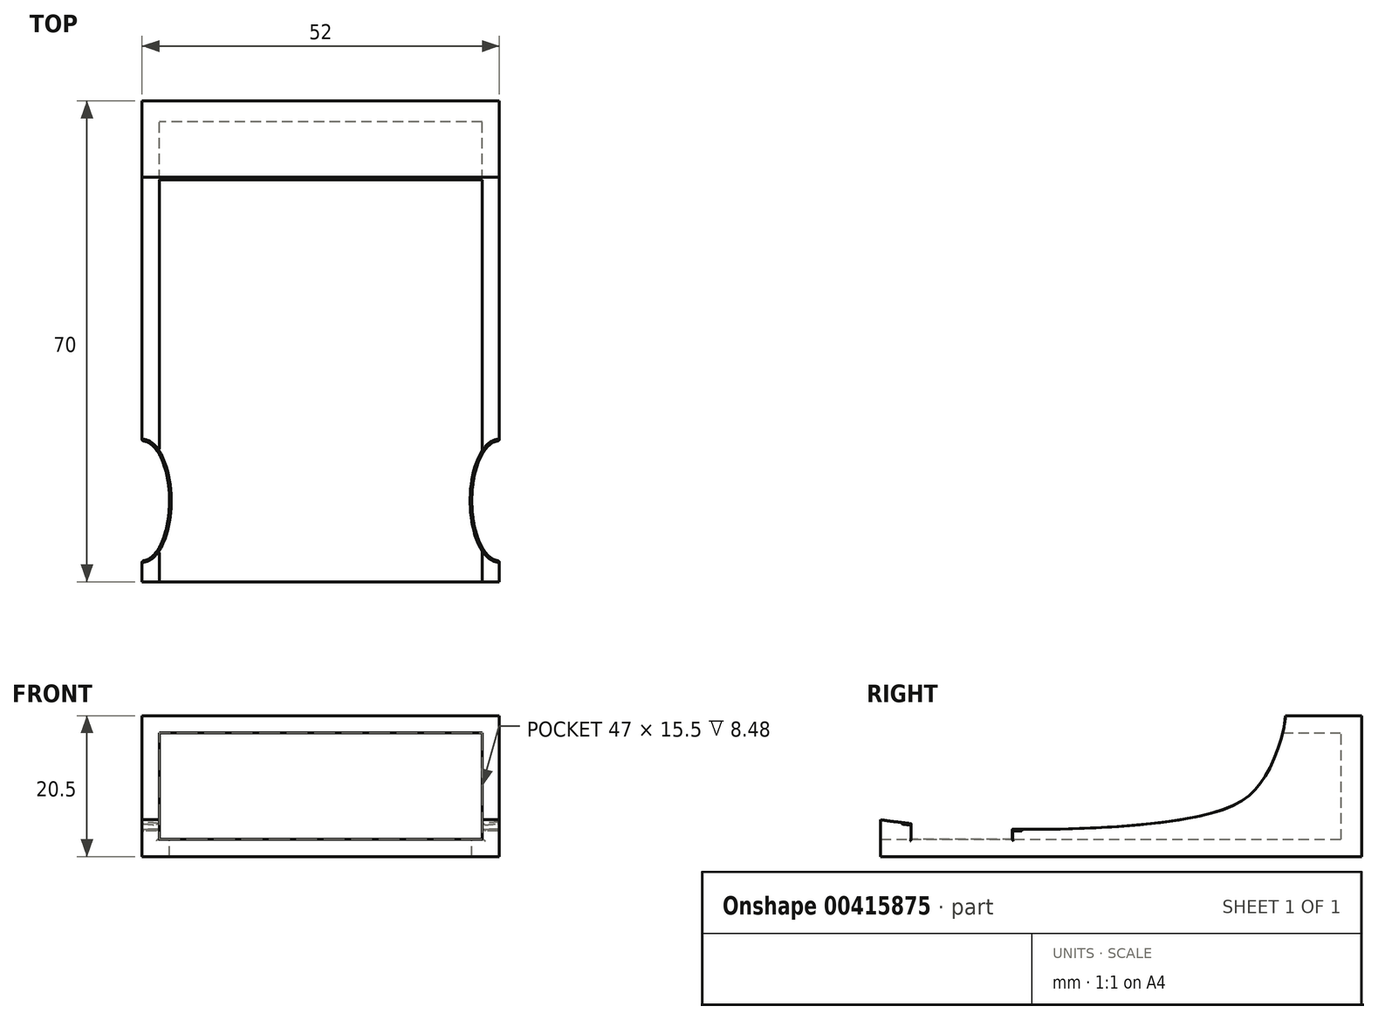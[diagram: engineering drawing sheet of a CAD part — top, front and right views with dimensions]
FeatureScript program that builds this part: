
annotation { "Feature Type Name" : "Feature", "Feature Type Description" : "" }
export const myFeature = defineFeature(function(context is Context, id is Id, definition is map)
    precondition{}
    {
        {
            var Q0;
            Q0=qCreatedBy(makeId("Front.planeOp"),FACE);
            var sketch = newSketch(context, id + "F0", { "sketchPlane" : qUnion([Q0])});
            skLineSegment(sketch, "E0.left", {"start": v(0, 0) * mm, "end": v(0, 0) * mm});
            skLineSegment(sketch, "E1", {"start": v(0, 0) * mm, "end": v(52, 0) * mm});
            skLineSegment(sketch, "E2", {"start": v(52, 0) * mm, "end": v(52, 20.5) * mm});
            skLineSegment(sketch, "E3", {"start": v(52, 20.5) * mm, "end": v(0, 20.5) * mm});
            skLineSegment(sketch, "E4", {"start": v(0, 20.5) * mm, "end": v(0, 0) * mm});
            skLineSegment(sketch, "E5", {"start": v(2.5, 2.5) * mm, "end": v(2.5, 18) * mm});
            skLineSegment(sketch, "E6", {"start": v(2.5, 18) * mm, "end": v(49.5, 18) * mm});
            skLineSegment(sketch, "E7", {"start": v(49.5, 18) * mm, "end": v(49.5, 2.5) * mm});
            skLineSegment(sketch, "E8", {"start": v(49.5, 2.5) * mm, "end": v(2.5, 2.5) * mm});
            skSolve(sketch);
        }
        {
            var Q0;
            Q0 = qSketchRegion(id + "F0", true);
            extrude(context, id + "F1", {"entities" : qUnion([Q0]), "depth" : 67 * mm});
        }
        {
            var Q0;
            Q0=makeQuery(id+"F0.imprint","IMPRINT",FACE,{"disambiguationData":[TD([[makeQuery(id+"F0.imprint","IMPRINT",EDGE,{"derivedFrom":sQuery(id+"F0.wireOp",EDGE,"E5")}),-1.0]])]});
            var Q1;
            Q1=makeQuery(id+"F0.imprint","IMPRINT",FACE,{"disambiguationData":[TD([[makeQuery(id+"F0.imprint","IMPRINT",EDGE,{"derivedFrom":sQuery(id+"F0.wireOp",EDGE,"E1")}),1.0]])]});
            extrude(context, id + "F2", {"entities" : qUnion([Q0, Q1]), "operationType" : NewBodyOperationType.ADD, "oppositeDirection" : true, "depth" : 3 * mm});
        }
        {
            var Q0;
            Q0=qCreatedBy(makeId("Right.planeOp"),FACE);
            var sketch = newSketch(context, id + "F3", { "sketchPlane" : qUnion([Q0])});
            skFitSpline(sketch, "E9", {"points": [v(-11.3, 29.1) * mm, v(-10.17, 13.31) * mm, v(-20.54, 5.9) * mm, v(-76.25, 7.4) * mm, v(-83.86, 15.4) * mm, v(-74.07, 28.56) * mm, v(-11.3, 29.1) * mm]});
            skSolve(sketch);
        }
        {
            var Q0;
            Q0=makeQuery(id+"F3.imprint","IMPRINT",FACE,{"disambiguationData":[TD([[makeQuery(id+"F3.imprint","IMPRINT",EDGE,{"derivedFrom":sQuery(id+"F3.wireOp",EDGE,"E9")}),-1.0]])]});
            extrude(context, id + "F4", {"entities" : qUnion([Q0]), "operationType" : NewBodyOperationType.REMOVE, "depth" : 70 * mm});
        }
        {
            var Q0;
            Q0=qCreatedBy(makeId("Top.planeOp"),FACE);
            var sketch = newSketch(context, id + "F5", { "sketchPlane" : qUnion([Q0])});
            skEllipse(sketch, "E10", {"center": v(0, -55.2) * mm, "majorRadius": 8.73 * mm, "minorRadius": 3.98 * mm, "majorAxis": v(0, -1)});
            skLineSegment(sketch, "E11", {"start": v(0, -55.2) * mm, "end": v(52, -55.2) * mm});
            skEllipse(sketch, "E12", {"center": v(52, -55.2) * mm, "majorRadius": 8.73 * mm, "minorRadius": 3.98 * mm, "majorAxis": v(0, -1)});
            skSolve(sketch);
        }
        {
            var Q0;
            Q0=makeQuery(id+"F5.imprint","IMPRINT",FACE,{"disambiguationData":[TD([[makeQuery(id+"F5.imprint","IMPRINT",EDGE,{"derivedFrom":sQuery(id+"F5.wireOp",EDGE,"E10")}),1.0]])]});
            var Q1;
            Q1=makeQuery(id+"F5.imprint","IMPRINT",FACE,{"disambiguationData":[TD([[makeQuery(id+"F5.imprint","IMPRINT",EDGE,{"derivedFrom":sQuery(id+"F5.wireOp",EDGE,"E12")}),1.0]])]});
            extrude(context, id + "F6", {"entities" : qUnion([Q0, Q1]), "operationType" : NewBodyOperationType.REMOVE, "depth" : 25 * mm});
        }
        {
            var Q0;
            Q0=makeQuery(id+"F6.boolean.opBoolean","INTERSECT",EDGE,{"derivedFrom":[makeQuery(id+"F1.opExtrude","SWEPT_FACE",FACE,{"disambiguationData":[OSD([sQuery(id+"F0.wireOp",EDGE,"E8")])]}),makeQuery(id+"F6.opExtrude","SWEPT_FACE",FACE,{"disambiguationData":[OSD([sQuery(id+"F5.wireOp",EDGE,"E10")])]})]});
            var Q1;
            Q1=makeQuery(id+"F6.boolean.opBoolean","INTERSECT",EDGE,{"disambiguationData":[OD(1.0)],"derivedFrom":[makeQuery(id+"F4.boolean.opBoolean","COPY",FACE,{"derivedFrom":makeQuery(id+"F4.opExtrude","SWEPT_FACE",FACE,{"disambiguationData":[OSD([sQuery(id+"F3.wireOp",EDGE,"E9")])]})}),makeQuery(id+"F6.opExtrude","SWEPT_FACE",FACE,{"disambiguationData":[OSD([sQuery(id+"F5.wireOp",EDGE,"E10")])]})]});
            var Q2;
            Q2=makeQuery(id+"F6.boolean.opBoolean","INTERSECT",EDGE,{"disambiguationData":[OD(0.0)],"derivedFrom":[makeQuery(id+"F4.boolean.opBoolean","COPY",FACE,{"derivedFrom":makeQuery(id+"F4.opExtrude","SWEPT_FACE",FACE,{"disambiguationData":[OSD([sQuery(id+"F3.wireOp",EDGE,"E9")])]})}),makeQuery(id+"F6.opExtrude","SWEPT_FACE",FACE,{"disambiguationData":[OSD([sQuery(id+"F5.wireOp",EDGE,"E10")])]})]});
            var Q3;
            Q3=makeQuery(id+"F6.boolean.opBoolean","INTERSECT",EDGE,{"disambiguationData":[OD(0.0)],"derivedFrom":[makeQuery(id+"F1.opExtrude","SWEPT_FACE",FACE,{"disambiguationData":[OSD([sQuery(id+"F0.wireOp",EDGE,"E5")])]}),makeQuery(id+"F6.opExtrude","SWEPT_FACE",FACE,{"disambiguationData":[OSD([sQuery(id+"F5.wireOp",EDGE,"E10")])]})]});
            var Q4;
            Q4=makeQuery(id+"F6.boolean.opBoolean","INTERSECT",EDGE,{"disambiguationData":[OD(1.0)],"derivedFrom":[makeQuery(id+"F4.boolean.opBoolean","COPY",FACE,{"derivedFrom":makeQuery(id+"F4.opExtrude","SWEPT_FACE",FACE,{"disambiguationData":[OSD([sQuery(id+"F3.wireOp",EDGE,"E9")])]})}),makeQuery(id+"F6.opExtrude","SWEPT_FACE",FACE,{"disambiguationData":[OSD([sQuery(id+"F5.wireOp",EDGE,"E12")])]})]});
            var Q5;
            Q5=makeQuery(id+"F6.boolean.opBoolean","INTERSECT",EDGE,{"derivedFrom":[makeQuery(id+"F1.opExtrude","SWEPT_FACE",FACE,{"disambiguationData":[OSD([sQuery(id+"F0.wireOp",EDGE,"E8")])]}),makeQuery(id+"F6.opExtrude","SWEPT_FACE",FACE,{"disambiguationData":[OSD([sQuery(id+"F5.wireOp",EDGE,"E12")])]})]});
            var Q6;
            Q6=makeQuery(id+"F6.boolean.opBoolean","INTERSECT",EDGE,{"disambiguationData":[OD(0.0)],"derivedFrom":[makeQuery(id+"F4.boolean.opBoolean","COPY",FACE,{"derivedFrom":makeQuery(id+"F4.opExtrude","SWEPT_FACE",FACE,{"disambiguationData":[OSD([sQuery(id+"F3.wireOp",EDGE,"E9")])]})}),makeQuery(id+"F6.opExtrude","SWEPT_FACE",FACE,{"disambiguationData":[OSD([sQuery(id+"F5.wireOp",EDGE,"E12")])]})]});
            var Q7;
            Q7=makeQuery(id+"F6.boolean.opBoolean","INTERSECT",EDGE,{"disambiguationData":[OD(1.0)],"derivedFrom":[makeQuery(id+"F1.opExtrude","SWEPT_FACE",FACE,{"disambiguationData":[OSD([sQuery(id+"F0.wireOp",EDGE,"E7")])]}),makeQuery(id+"F6.opExtrude","SWEPT_FACE",FACE,{"disambiguationData":[OSD([sQuery(id+"F5.wireOp",EDGE,"E12")])]})]});
            var Q8;
            Q8=makeQuery(id+"F6.boolean.opBoolean","INTERSECT",EDGE,{"disambiguationData":[OD(0.0)],"derivedFrom":[makeQuery(id+"F1.opExtrude","SWEPT_FACE",FACE,{"disambiguationData":[OSD([sQuery(id+"F0.wireOp",EDGE,"E7")])]}),makeQuery(id+"F6.opExtrude","SWEPT_FACE",FACE,{"disambiguationData":[OSD([sQuery(id+"F5.wireOp",EDGE,"E12")])]})]});
            var Q9;
            Q9=makeQuery(id+"F6.boolean.opBoolean","COPY",EDGE,{"derivedFrom":makeQuery(id+"F6.opExtrude","CAP_EDGE",EDGE,{"disambiguationData":[OSD([sQuery(id+"F5.wireOp",EDGE,"E12")])],"isStart":true})});
            var Q10;
            {var subQ0=sQuery(id+"F0.wireOp",EDGE,"E2");Q10=makeQuery(id+"F6.boolean.opBoolean","INTERSECT",EDGE,{"disambiguationData":[OD(0.0)],"derivedFrom":[makeQuery(id+"F2.boolean.opBoolean","MERGE",FACE,{"derivedFrom":[makeQuery(id+"F1.opExtrude","SWEPT_FACE",FACE,{"disambiguationData":[OSD([subQ0])]}),makeQuery(id+"F2.opExtrude","SWEPT_FACE",FACE,{"disambiguationData":[OSD([subQ0])]})]}),makeQuery(id+"F6.opExtrude","SWEPT_FACE",FACE,{"disambiguationData":[OSD([sQuery(id+"F5.wireOp",EDGE,"E12")])]})]});}
            var Q11;
            {var subQ0=sQuery(id+"F0.wireOp",EDGE,"E2");Q11=makeQuery(id+"F6.boolean.opBoolean","INTERSECT",EDGE,{"disambiguationData":[OD(1.0)],"derivedFrom":[makeQuery(id+"F2.boolean.opBoolean","MERGE",FACE,{"derivedFrom":[makeQuery(id+"F1.opExtrude","SWEPT_FACE",FACE,{"disambiguationData":[OSD([subQ0])]}),makeQuery(id+"F2.opExtrude","SWEPT_FACE",FACE,{"disambiguationData":[OSD([subQ0])]})]}),makeQuery(id+"F6.opExtrude","SWEPT_FACE",FACE,{"disambiguationData":[OSD([sQuery(id+"F5.wireOp",EDGE,"E12")])]})]});}
            var Q12;
            Q12=makeQuery(id+"F6.boolean.opBoolean","COPY",EDGE,{"derivedFrom":makeQuery(id+"F6.opExtrude","CAP_EDGE",EDGE,{"disambiguationData":[OSD([sQuery(id+"F5.wireOp",EDGE,"E10")])],"isStart":true})});
            var Q13;
            {var subQ0=sQuery(id+"F0.wireOp",EDGE,"E4");Q13=makeQuery(id+"F6.boolean.opBoolean","INTERSECT",EDGE,{"disambiguationData":[OD(0.0)],"derivedFrom":[makeQuery(id+"F2.boolean.opBoolean","MERGE",FACE,{"derivedFrom":[makeQuery(id+"F1.opExtrude","SWEPT_FACE",FACE,{"disambiguationData":[OSD([subQ0])]}),makeQuery(id+"F2.opExtrude","SWEPT_FACE",FACE,{"disambiguationData":[OSD([subQ0])]})]}),makeQuery(id+"F6.opExtrude","SWEPT_FACE",FACE,{"disambiguationData":[OSD([sQuery(id+"F5.wireOp",EDGE,"E10")])]})]});}
            var Q14;
            {var subQ0=sQuery(id+"F0.wireOp",EDGE,"E4");Q14=makeQuery(id+"F6.boolean.opBoolean","INTERSECT",EDGE,{"disambiguationData":[OD(1.0)],"derivedFrom":[makeQuery(id+"F2.boolean.opBoolean","MERGE",FACE,{"derivedFrom":[makeQuery(id+"F1.opExtrude","SWEPT_FACE",FACE,{"disambiguationData":[OSD([subQ0])]}),makeQuery(id+"F2.opExtrude","SWEPT_FACE",FACE,{"disambiguationData":[OSD([subQ0])]})]}),makeQuery(id+"F6.opExtrude","SWEPT_FACE",FACE,{"disambiguationData":[OSD([sQuery(id+"F5.wireOp",EDGE,"E10")])]})]});}
            var Q15;
            Q15=makeQuery(id+"F6.boolean.opBoolean","INTERSECT",EDGE,{"disambiguationData":[OD(1.0)],"derivedFrom":[makeQuery(id+"F1.opExtrude","SWEPT_FACE",FACE,{"disambiguationData":[OSD([sQuery(id+"F0.wireOp",EDGE,"E5")])]}),makeQuery(id+"F6.opExtrude","SWEPT_FACE",FACE,{"disambiguationData":[OSD([sQuery(id+"F5.wireOp",EDGE,"E10")])]})]});
            fillet(context, id + "F7", {"entities" : qUnion([Q0, Q1, Q2, Q3, Q4, Q5, Q6, Q7, Q8, Q9, Q10, Q11, Q12, Q13, Q14, Q15]), "radius" : .25 * mm, "tangentPropagation" : true, "allowEdgeOverflow" : false});
        }
    });
